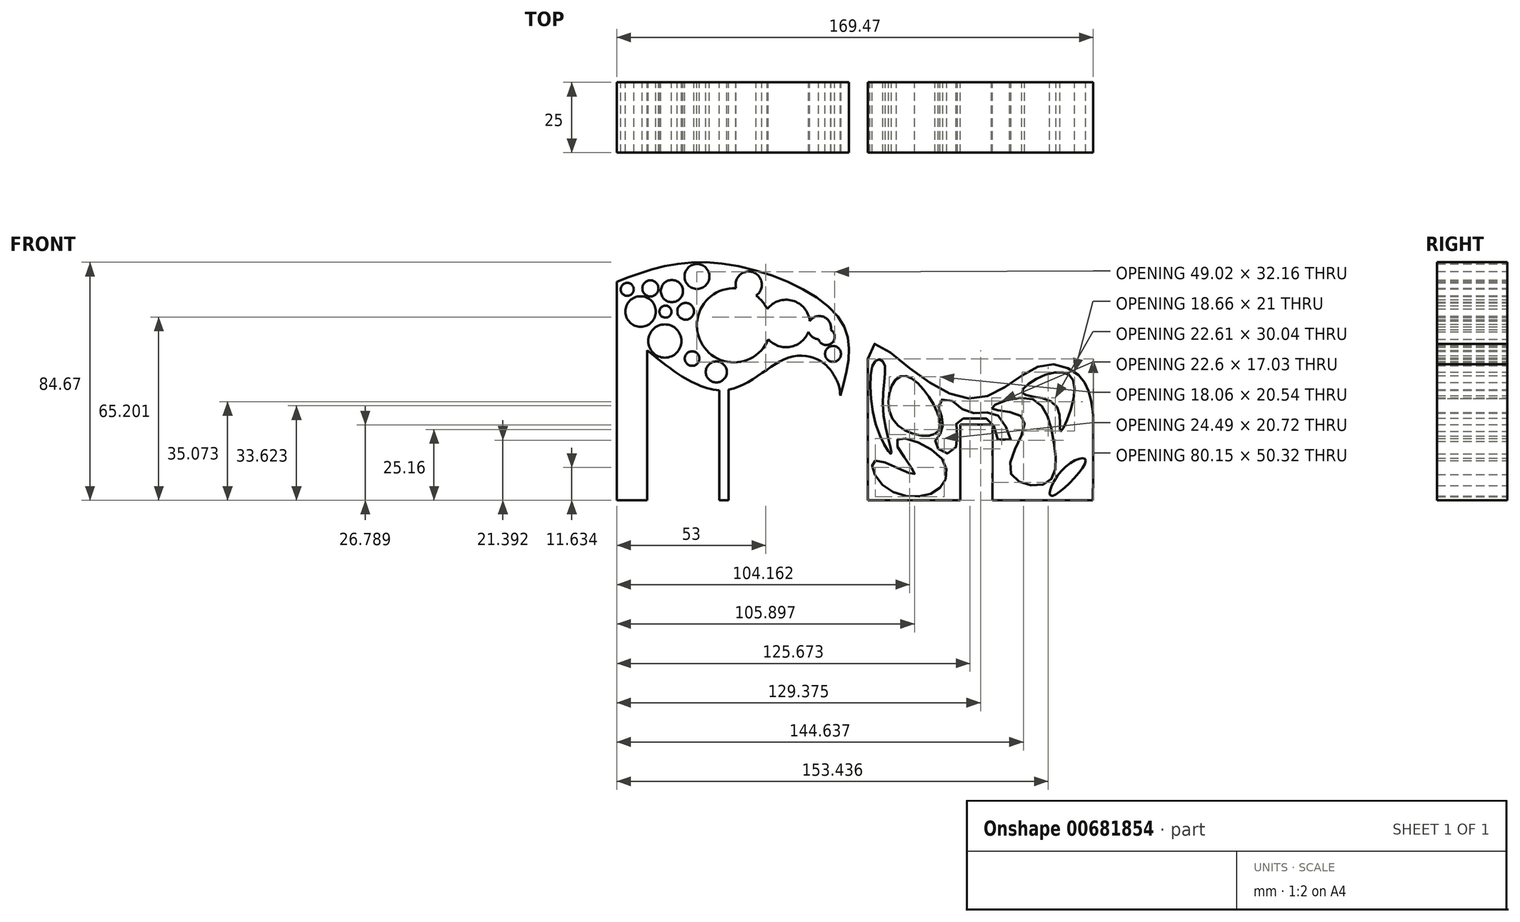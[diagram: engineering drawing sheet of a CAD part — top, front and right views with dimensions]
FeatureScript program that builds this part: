
annotation { "Feature Type Name" : "Feature", "Feature Type Description" : "" }
export const myFeature = defineFeature(function(context is Context, id is Id, definition is map)
    precondition{}
    {
        {
            var Q0;
            Q0=qCreatedBy(makeId("Front.planeOp"),FACE);
            var sketch = newSketch(context, id + "F0", { "sketchPlane" : qUnion([Q0])});
            skLineSegment(sketch, "E0", {"start": v(0, 0) * mm, "end": v(80, 0) * mm});
            skLineSegment(sketch, "E1", {"start": v(0, 0) * mm, "end": v(0, 50.32) * mm});
            skFitSpline(sketch, "E2", {"points": [v(0, 50.32) * mm, v(10.82, 50.32) * mm, v(39.7, 36.3) * mm, v(61.7, 47.92) * mm, v(74.5, 44.94) * mm, v(78.15, 39.7) * mm, v(79.75, 33.98) * mm, v(80.07, 30.3) * mm, v(80.12, 27.52) * mm, v(80, 0) * mm], "startDerivative": vector(0, 264.56) * mm, "endDerivative": vector(-4.14, -191.46) * mm});
            skFitSpline(sketch, "E3", {"points": [v(2.62, 49.56) * mm, v(3.08, 26.21) * mm, v(8.34, 16.6) * mm, v(5.37, 32.4) * mm, v(5.6, 49.1) * mm, v(2.62, 49.56) * mm]});
            skFitSpline(sketch, "E4", {"points": [v(2.62, 14.08) * mm, v(16.58, 9.27) * mm, v(10.17, 20.95) * mm, v(25.97, 15.22) * mm, v(24.6, 3.55) * mm, v(5.82, 4.92) * mm, v(2.62, 14.08) * mm]});
            skFitSpline(sketch, "E5", {"points": [v(8.8, 28.96) * mm, v(24.14, 23.7) * mm, v(23.22, 34.45) * mm, v(11.55, 44.07) * mm, v(8.8, 28.96) * mm]});
            skLineSegment(sketch, "E6.bottom", {"start": v(32.84, 0) * mm, "end": v(44.28, 0) * mm});
            skLineSegment(sketch, "E6.top", {"start": v(32.84, 26.9) * mm, "end": v(44.28, 26.9) * mm});
            skLineSegment(sketch, "E6.left", {"start": v(32.84, 0) * mm, "end": v(32.84, 26.9) * mm});
            skLineSegment(sketch, "E6.right", {"start": v(44.28, 0) * mm, "end": v(44.28, 26.9) * mm});
            skFitSpline(sketch, "E7", {"points": [v(25.07, 18.27) * mm, v(27.97, 16.56) * mm, v(31.06, 18.54) * mm, v(31.79, 22.22) * mm, v(31.4, 26.9) * mm, v(32.84, 28.74) * mm, v(36.26, 29.14) * mm, v(40.41, 29.14) * mm, v(44.5, 27.88) * mm, v(45.74, 22.1) * mm, v(50.75, 21.56) * mm, v(48.64, 26.9) * mm, v(45.42, 30.65) * mm, v(40.74, 31.18) * mm, v(35.67, 31.3) * mm, v(31.46, 34.14) * mm, v(27.77, 36.25) * mm, v(25.14, 34.6) * mm, v(25.4, 32.23) * mm, v(26.39, 29.27) * mm, v(26.65, 26.9) * mm, v(26.06, 24.13) * mm, v(25.14, 22.95) * mm, v(23.82, 20.7) * mm, v(25.07, 18.27) * mm]});
            skFitSpline(sketch, "E8", {"points": [v(44.03, 32.7) * mm, v(55.36, 29.07) * mm, v(50.55, 10.37) * mm, v(63.72, 6.16) * mm, v(65.9, 22.16) * mm, v(57.27, 36.3) * mm, v(44.03, 32.7) * mm]});
            skFitSpline(sketch, "E9", {"points": [v(54.8, 38.24) * mm, v(66.8, 33.84) * mm, v(68.53, 24.52) * mm, v(73.52, 40.37) * mm, v(66.06, 45.43) * mm, v(54.8, 38.24) * mm]});
            skFitSpline(sketch, "E10", {"points": [v(77.5, 14.06) * mm, v(65.34, 1.55) * mm, v(69.75, 11.44) * mm, v(77.5, 14.06) * mm]});
            skLineSegment(sketch, "E11", {"start": v(-89.3, 53.37) * mm, "end": v(-89.3, 77.78) * mm});
            skFitSpline(sketch, "E12", {"points": [v(-89.3, 77.78) * mm, v(-54.57, 84.47) * mm, v(-9.54, 63.78) * mm, v(-9.8, 37.17) * mm], "startDerivative": vector(95.08, 35.85) * mm, "endDerivative": vector(-27.2, -98.04) * mm});
            skCircle(sketch, "E13", {"center": v(-85.56, 75.01) * mm, "radius": 2.32 * mm});
            skCircle(sketch, "E14", {"center": v(-80.83, 67.14) * mm, "radius": 5.43 * mm});
            skCircle(sketch, "E15", {"center": v(-72.2, 56.64) * mm, "radius": 5.91 * mm});
            skCircle(sketch, "E16", {"center": v(-72, 67.1) * mm, "radius": 2.14 * mm});
            skCircle(sketch, "E17", {"center": v(-77.35, 75.36) * mm, "radius": 2.87 * mm});
            skCircle(sketch, "E18", {"center": v(-69.7, 74.42) * mm, "radius": 3.95 * mm});
            skCircle(sketch, "E19", {"center": v(-47.63, 62.25) * mm, "radius": 13.18 * mm});
            skCircle(sketch, "E20", {"center": v(-60.77, 79.6) * mm, "radius": 4.43 * mm});
            skCircle(sketch, "E21", {"center": v(-64.8, 67.23) * mm, "radius": 2.97 * mm});
            skCircle(sketch, "E22", {"center": v(-62.52, 50.4) * mm, "radius": 2.6 * mm});
            skCircle(sketch, "E23", {"center": v(-53.9, 45.64) * mm, "radius": 3.75 * mm});
            skCircle(sketch, "E24", {"center": v(-29.07, 62.9) * mm, "radius": 8.44 * mm});
            skCircle(sketch, "E25", {"center": v(-42.37, 76.71) * mm, "radius": 4.67 * mm});
            skCircle(sketch, "E26", {"center": v(-12.4, 52.06) * mm, "radius": 2.83 * mm});
            skCircle(sketch, "E27", {"center": v(-17.26, 61.4) * mm, "radius": 4.13 * mm});
            skCircle(sketch, "E28", {"center": v(-14.72, 58.13) * mm, "radius": 2.93 * mm});
            skLineSegment(sketch, "E29", {"start": v(-89.3, 53.37) * mm, "end": v(-89.3, 0) * mm});
            skLineSegment(sketch, "E30", {"start": v(-89.3, 0) * mm, "end": v(-78.48, 0) * mm});
            skLineSegment(sketch, "E31", {"start": v(-78.48, 0) * mm, "end": v(-78.48, 53.37) * mm});
            skLineSegment(sketch, "E32", {"start": v(-49.6, 39.34) * mm, "end": v(-49.6, 0) * mm});
            skLineSegment(sketch, "E33", {"start": v(-49.6, 0) * mm, "end": v(-52.81, 0) * mm});
            skLineSegment(sketch, "E34", {"start": v(-52.81, 0) * mm, "end": v(-52.81, 39.2) * mm});
            skFitSpline(sketch, "E35", {"points": [v(-89.3, 53.37) * mm, v(-78.48, 53.37) * mm, v(-49.6, 39.34) * mm, v(-27.6, 50.97) * mm, v(-14.8, 47.99) * mm, v(-11.15, 42.74) * mm, v(-9.8, 37.17) * mm, v(-10.76, -30) * mm], "startDerivative": vector(0, 264.56) * mm, "endDerivative": vector(-21.41, 0) * mm});
            skLineSegment(sketch, "E36", {"start": v(-9.8, 37.17) * mm, "end": v(-9.8, 0) * mm});
            skLineSegment(sketch, "E37", {"start": v(-9.8, 0) * mm, "end": v(-15, 0) * mm});
            skLineSegment(sketch, "E38", {"start": v(-15, 0) * mm, "end": v(-14.8, 47.99) * mm});
            skSolve(sketch);
        }
        {
            var Q0;
            {var subQ2=sQuery(id+"F0.wireOp",EDGE,"E1");Q0=makeQuery(id+"F0.imprint","IMPRINT",FACE,{"disambiguationData":[TD([[makeQuery(id+"F0.imprint","IMPRINT",EDGE,{"derivedFrom":subQ2}),-1.0]])]});}
            extrude(context, id + "F1", {"entities" : qUnion([Q0]), "depth" : 25 * mm, "offsetDistance" : 25 * mm});
        }
        {
            var Q0;
            {var subQ0=sQuery(id+"F0.wireOp",EDGE,"E11");Q0=makeQuery(id+"F0.imprint","IMPRINT",FACE,{"disambiguationData":[TD([[makeQuery(id+"F0.imprint","IMPRINT",EDGE,{"derivedFrom":subQ0}),-1.0]])]});}
            extrude(context, id + "F2", {"entities" : qUnion([Q0]), "depth" : 25 * mm, "offsetDistance" : 25 * mm});
        }
        {
            var Q0;
            {var subQ0=sQuery(id+"F0.wireOp",EDGE,"l7crcCJq-xI0m-HVP2-zSkE-767ge4gfVtzM");Q0=makeQuery(id+"F0.imprint","IMPRINT",FACE,{"disambiguationData":[TD([[makeQuery(id+"F0.imprint","IMPRINT",EDGE,{"derivedFrom":subQ0}),-1.0]])]});}
            var Q1;
            {var subQ0=sQuery(id+"F0.wireOp",EDGE,"E32");Q1=makeQuery(id+"F0.imprint","IMPRINT",FACE,{"disambiguationData":[TD([[makeQuery(id+"F0.imprint","IMPRINT",EDGE,{"derivedFrom":subQ0}),-1.0]])]});}
            var Q2;
            {var subQ0=sQuery(id+"F0.wireOp",EDGE,"E29");Q2=makeQuery(id+"F0.imprint","IMPRINT",FACE,{"disambiguationData":[TD([[makeQuery(id+"F0.imprint","IMPRINT",EDGE,{"derivedFrom":subQ0}),1.0]])]});}
            extrude(context, id + "F3", {"entities" : qUnion([Q0, Q1, Q2]), "operationType" : NewBodyOperationType.ADD, "depth" : 25 * mm, "offsetDistance" : 25 * mm});
        }
    });
